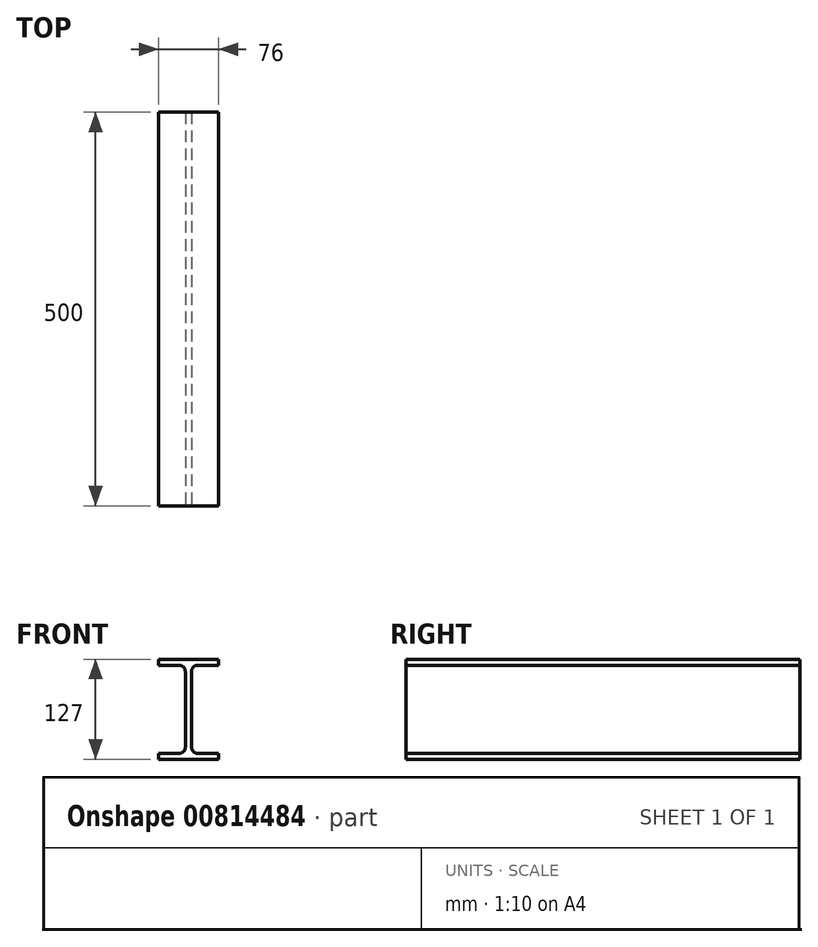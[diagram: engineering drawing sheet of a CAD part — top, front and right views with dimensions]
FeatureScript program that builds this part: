
annotation { "Feature Type Name" : "Feature", "Feature Type Description" : "" }
export const myFeature = defineFeature(function(context is Context, id is Id, definition is map)
    precondition{}
    {
        {
            var Q0;
            Q0=qCreatedBy(makeId("Front.planeOp"),FACE);
            var sketch = newSketch(context, id + "F0", { "sketchPlane" : qUnion([Q0])});
            skLineSegment(sketch, "E0", {"start": v(0, 0) * mm, "end": v(4, 0) * mm, "construction": true});
            skLineSegment(sketch, "E1", {"start": v(4, 0) * mm, "end": v(4, 48.3) * mm});
            skLineSegment(sketch, "E2", {"start": v(11.6, 55.9) * mm, "end": v(38, 55.9) * mm});
            skLineSegment(sketch, "E3", {"start": v(38, 55.9) * mm, "end": v(38, 63.5) * mm});
            skLineSegment(sketch, "E4", {"start": v(38, 63.5) * mm, "end": v(0, 63.5) * mm});
            skLineSegment(sketch, "E5", {"start": v(0, 63.5) * mm, "end": v(0, 0) * mm, "construction": true});
            skLineSegment(sketch, "E6.MirrorCS", {"start": v(-38, 63.5) * mm, "end": v(0, 63.5) * mm});
            skLineSegment(sketch, "E7.MirrorCS", {"start": v(-38, 55.9) * mm, "end": v(-38, 63.5) * mm});
            skLineSegment(sketch, "E8.MirrorCS", {"start": v(-11.6, 55.9) * mm, "end": v(-38, 55.9) * mm});
            skLineSegment(sketch, "E9.MirrorCS", {"start": v(-4, 0) * mm, "end": v(-4, 48.3) * mm});
            skPoint(sketch, "E10.visualSharp", {"position": v(4, 55.9) * mm});
            skArc(sketch, "E10.filletArc", {"start": v(11.6, 55.9) * mm, "mid": v(6.23, 53.67) * mm, "end": v(4, 48.3) * mm});
            skPoint(sketch, "E11.visualSharp", {"position": v(-4, 55.9) * mm});
            skArc(sketch, "E11.filletArc", {"start": v(-4, 48.3) * mm, "mid": v(-6.23, 53.67) * mm, "end": v(-11.6, 55.9) * mm});
            skArc(sketch, "E12.MirrorCS", {"start": v(11.6, -55.9) * mm, "mid": v(6.23, -53.67) * mm, "end": v(4, -48.3) * mm});
            skLineSegment(sketch, "E13.MirrorCS", {"start": v(-38, -55.9) * mm, "end": v(-38, -63.5) * mm});
            skLineSegment(sketch, "E14.MirrorCS", {"start": v(38, -55.9) * mm, "end": v(38, -63.5) * mm});
            skArc(sketch, "E15.MirrorCS", {"start": v(-4, -48.3) * mm, "mid": v(-6.23, -53.67) * mm, "end": v(-11.6, -55.9) * mm});
            skLineSegment(sketch, "E16.MirrorCS", {"start": v(0, -63.5) * mm, "end": v(0, 0) * mm, "construction": true});
            skPoint(sketch, "E17.MirrorP", {"position": v(-4, -55.9) * mm});
            skPoint(sketch, "E18.MirrorP", {"position": v(4, -55.9) * mm});
            skLineSegment(sketch, "E19.MirrorCS", {"start": v(4, 0) * mm, "end": v(4, -48.3) * mm});
            skLineSegment(sketch, "E20.MirrorCS", {"start": v(38, -63.5) * mm, "end": v(0, -63.5) * mm});
            skLineSegment(sketch, "E21.MirrorCS", {"start": v(-38, -63.5) * mm, "end": v(0, -63.5) * mm});
            skLineSegment(sketch, "E22.MirrorCS", {"start": v(-11.6, -55.9) * mm, "end": v(-38, -55.9) * mm});
            skLineSegment(sketch, "E23.MirrorCS", {"start": v(11.6, -55.9) * mm, "end": v(38, -55.9) * mm});
            skLineSegment(sketch, "E24.MirrorCS", {"start": v(-4, 0) * mm, "end": v(-4, -48.3) * mm});
            skSolve(sketch);
        }
        {
            var Q0;
            Q0=makeQuery(id+"F0.imprint","IMPRINT",FACE,{"disambiguationData":[TD([[makeQuery(id+"F0.imprint","IMPRINT",EDGE,{"derivedFrom":sQuery(id+"F0.wireOp",EDGE,"E1")}),1.0]])]});
            extrude(context, id + "F1", {"entities" : qUnion([Q0]), "oppositeDirection" : true, "depth" : 500 * mm, "offsetDistance" : 25 * mm});
        }
    });
